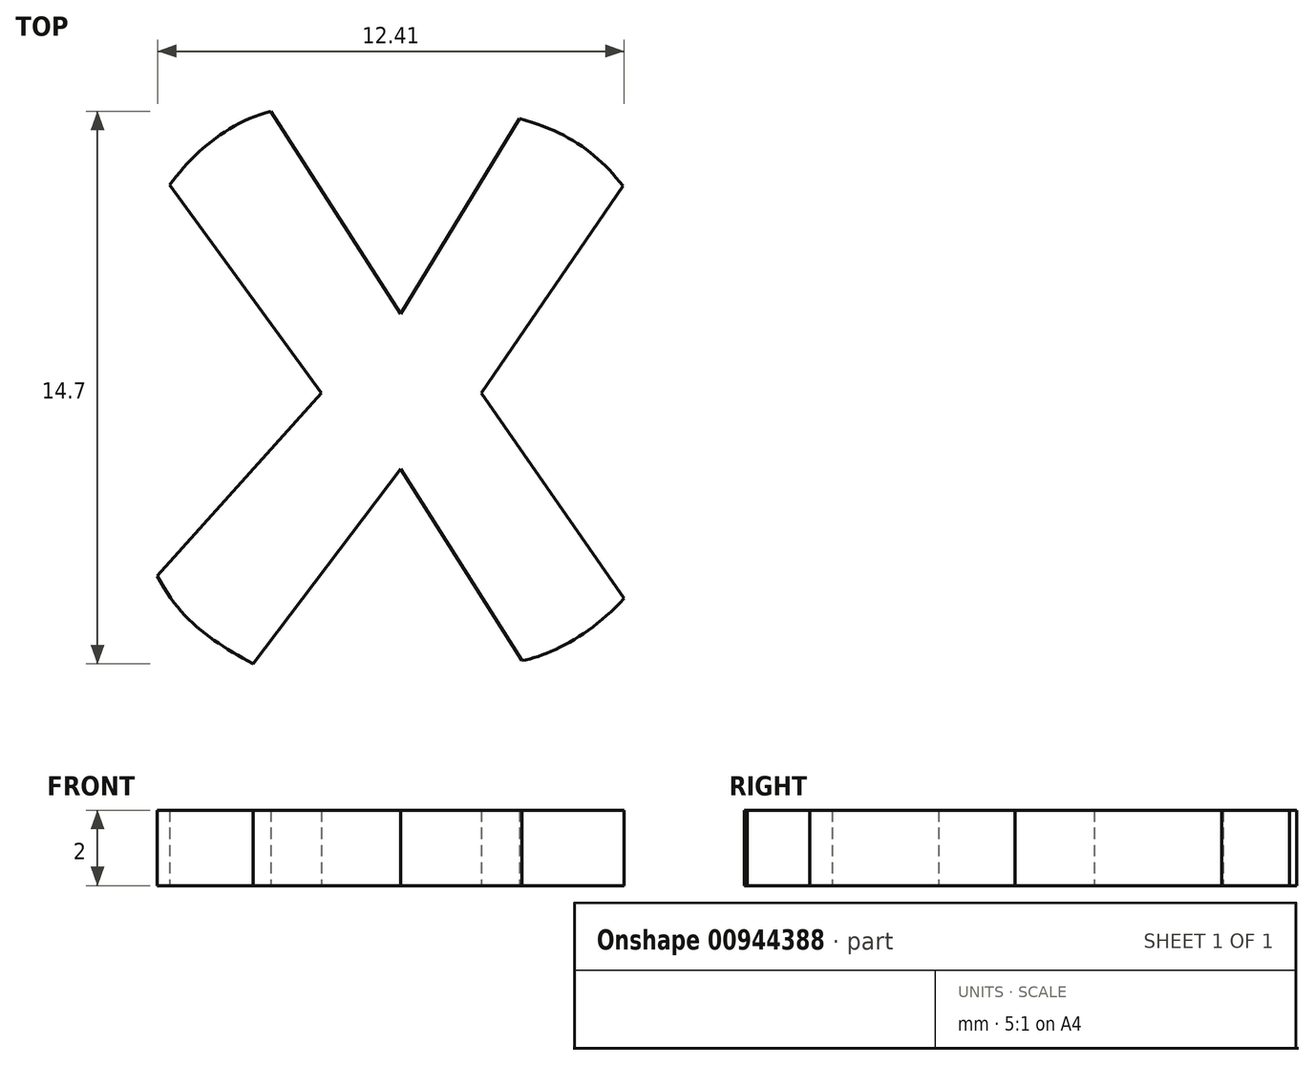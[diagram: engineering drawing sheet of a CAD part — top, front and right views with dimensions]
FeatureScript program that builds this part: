
annotation { "Feature Type Name" : "Feature", "Feature Type Description" : "" }
export const myFeature = defineFeature(function(context is Context, id is Id, definition is map)
    precondition{}
    {
        {
            var Q0;
            Q0=qCreatedBy(makeId("Top.planeOp"),FACE);
            var sketch = newSketch(context, id + "F0", { "sketchPlane" : qUnion([Q0])});
            skCircle(sketch, "E0", {"center": v(0.1, -0.08) * mm, "radius": 9 * mm});
            skLineSegment(sketch, "E1", {"start": v(0.1, -9.08) * mm, "end": v(0.1, 8.92) * mm, "construction": true});
            skLineSegment(sketch, "E2", {"start": v(-8.9, -0.08) * mm, "end": v(9.1, -0.08) * mm, "construction": true});
            skLineSegment(sketch, "E3", {"start": v(0.1, 2.03) * mm, "end": v(-3.75, 8.05) * mm});
            skLineSegment(sketch, "E4", {"start": v(0.1, 2.03) * mm, "end": v(3.82, 8.11) * mm});
            skLineSegment(sketch, "E5", {"start": v(0.1, -2.1) * mm, "end": v(-4.3, -7.93) * mm});
            skLineSegment(sketch, "E6", {"start": v(0.1, -2.1) * mm, "end": v(3.98, -8.2) * mm});
            skLineSegment(sketch, "E7", {"start": v(-2, -0.08) * mm, "end": v(-6.48, 6.05) * mm});
            skLineSegment(sketch, "E8", {"start": v(-2, -0.08) * mm, "end": v(-6.98, -5.63) * mm});
            skLineSegment(sketch, "E9", {"start": v(2.25, -0.08) * mm, "end": v(6.55, 6.2) * mm});
            skLineSegment(sketch, "E10", {"start": v(2.25, -0.08) * mm, "end": v(6.6, -6.32) * mm});
            skFitSpline(sketch, "E11", {"points": [v(-3.34, 7.42) * mm, v(-6.04, 5.46) * mm], "startDerivative": vector(-3.47, -0.92) * mm, "endDerivative": vector(-2.08, -2.73) * mm});
            skFitSpline(sketch, "E12", {"points": [v(-6.36, -4.94) * mm, v(-3.82, -7.28) * mm], "startDerivative": vector(1.88, -3.7) * mm, "endDerivative": vector(3.22, -1.82) * mm});
            skFitSpline(sketch, "E13", {"points": [v(3.34, -7.2) * mm, v(6.05, -5.54) * mm], "startDerivative": vector(2.31, 0.43) * mm, "endDerivative": vector(2.57, 2.85) * mm});
            skFitSpline(sketch, "E14", {"points": [v(6.02, 5.43) * mm, v(3.28, 7.22) * mm], "startDerivative": vector(-2.05, 2.67) * mm, "endDerivative": vector(-3.82, 1.07) * mm});
            skSolve(sketch);
        }
        {
            var Q0;
            {var subQ0=sQuery(id+"F0.wireOp",EDGE,"E11");Q0=makeQuery(id+"F0.imprint","IMPRINT",FACE,{"disambiguationData":[TD([[makeQuery(id+"F0.imprint","IMPRINT",EDGE,{"derivedFrom":subQ0}),1.0]])]});}
            extrude(context, id + "F1", {"entities" : qUnion([Q0]), "depth" : 2 * mm, "offsetDistance" : 25 * mm});
        }
    });
